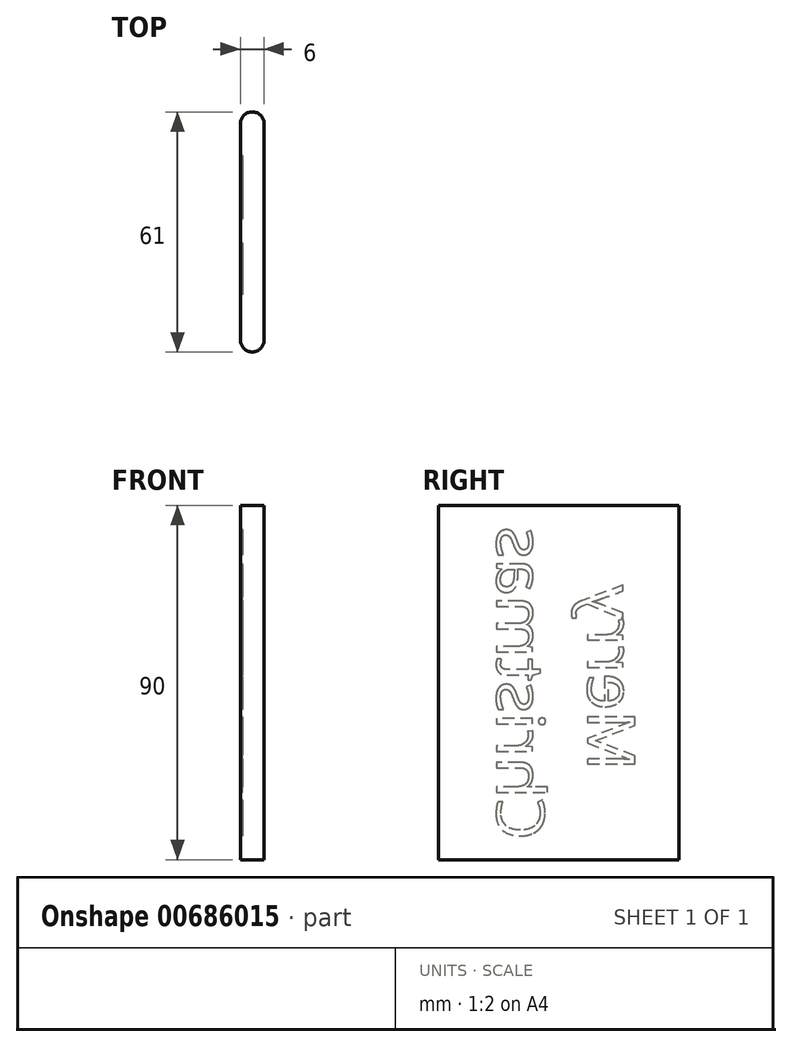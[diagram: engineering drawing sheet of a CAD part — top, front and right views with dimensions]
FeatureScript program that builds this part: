
annotation { "Feature Type Name" : "Feature", "Feature Type Description" : "" }
export const myFeature = defineFeature(function(context is Context, id is Id, definition is map)
    precondition{}
    {
        {
            var Q0;
            Q0=qCreatedBy(makeId("Top.planeOp"),FACE);
            var sketch = newSketch(context, id + "F0", { "sketchPlane" : qUnion([Q0])});
            skLineSegment(sketch, "E0.left", {"start": v(-1, 27.5) * mm, "end": v(-1, -27.5) * mm, "construction": true});
            skLineSegment(sketch, "E0.right", {"start": v(1, 27.5) * mm, "end": v(1, -27.5) * mm, "construction": true});
            skPoint(sketch, "E0.middle", {"position": v(0, 0) * mm});
            skArc(sketch, "E1", {"start": v(-1, 27.5) * mm, "mid": v(0, 28.5) * mm, "end": v(1, 27.5) * mm, "construction": true});
            skArc(sketch, "E2", {"start": v(1, -27.5) * mm, "mid": v(0, -28.5) * mm, "end": v(-1, -27.5) * mm, "construction": true});
            skLineSegment(sketch, "E3.0", {"start": v(-3, 27.5) * mm, "end": v(-3, -27.5) * mm});
            skArc(sketch, "E3.1", {"start": v(-3, 27.5) * mm, "mid": v(0, 30.5) * mm, "end": v(3, 27.5) * mm});
            skLineSegment(sketch, "E3.2", {"start": v(3, 27.5) * mm, "end": v(3, -27.5) * mm});
            skArc(sketch, "E3.3", {"start": v(3, -27.5) * mm, "mid": v(0, -30.5) * mm, "end": v(-3, -27.5) * mm});
            skSolve(sketch);
        }
        {
            var Q0;
            Q0=makeQuery(id+"F0.imprint","IMPRINT",FACE,{"disambiguationData":[TD([[makeQuery(id+"F0.imprint","IMPRINT",EDGE,{"derivedFrom":sQuery(id+"F0.wireOp",EDGE,"E3.0")}),1.0]])]});
            extrude(context, id + "F1", {"entities" : qUnion([Q0]), "depth" : 90 * mm, "offsetDistance" : 25 * mm});
        }
        {
            var Q0;
            Q0=makeQuery(id+"F1.opExtrude","SWEPT_FACE",FACE,{"disambiguationData":[OSD([sQuery(id+"F0.wireOp",EDGE,"E3.0")])]});
            var sketch = newSketch(context, id + "F2", { "sketchPlane" : qUnion([Q0])});
            skText(sketch, "E4", { "text": "    Merry\nChristmas", "fontName": "OpenSans-Regular.ttf"});
            const initialGuessF2  = {"E4": [-0.0073, 0.005, 0, 1, 0.0122]};
            skSetInitialGuess(sketch, initialGuessF2);
            skSolve(sketch);
        }
        {
            var Q0;
            Q0 = qSketchRegion(id + "F2", true);
            extrude(context, id + "F3", {"entities" : qUnion([Q0]), "operationType" : NewBodyOperationType.REMOVE, "oppositeDirection" : true, "depth" : 0.5 * mm, "offsetDistance" : 25 * mm});
        }
    });
